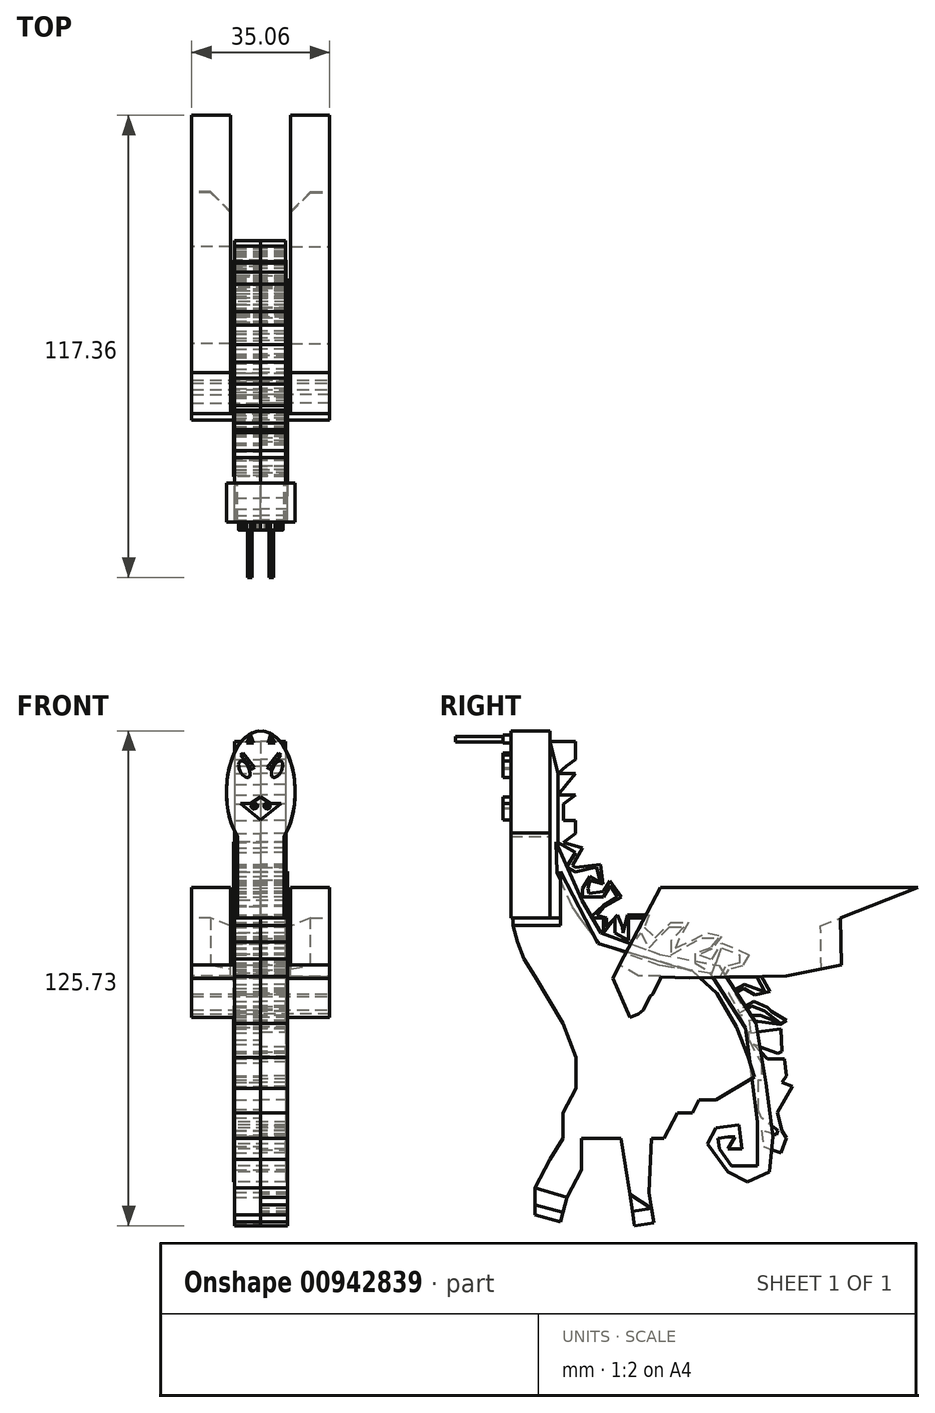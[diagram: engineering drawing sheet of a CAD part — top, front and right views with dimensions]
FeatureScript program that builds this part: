
annotation { "Feature Type Name" : "Feature", "Feature Type Description" : "" }
export const myFeature = defineFeature(function(context is Context, id is Id, definition is map)
    precondition{}
    {
        {
            var Q0;
            Q0=qCreatedBy(makeId("Front.planeOp"),FACE);
            var sketch = newSketch(context, id + "F0", { "sketchPlane" : qUnion([Q0])});
            skEllipse(sketch, "E0", {"center": v(0, 32.09) * mm, "majorRadius": 15.5 * mm, "minorRadius": 8.74 * mm, "majorAxis": v(0, -1)});
            skLineSegment(sketch, "E1", {"start": v(-6.45, 21.64) * mm, "end": v(-6.45, 0) * mm});
            skLineSegment(sketch, "E2", {"start": v(-6.45, 0) * mm, "end": v(5.95, 0) * mm});
            skLineSegment(sketch, "E3", {"start": v(5.95, 0) * mm, "end": v(5.95, 20.74) * mm});
            skSolve(sketch);
        }
        {
            var Q0;
            Q0=qCreatedBy(makeId("Front.planeOp"),FACE);
            var sketch = newSketch(context, id + "F1", { "sketchPlane" : qUnion([Q0])});
            skLineSegment(sketch, "E4", {"start": v(0, 30.81) * mm, "end": v(-2.55, 29.11) * mm});
            skLineSegment(sketch, "E5", {"start": v(-2.55, 29.11) * mm, "end": v(-5.1, 29.11) * mm});
            skLineSegment(sketch, "E6", {"start": v(-5.1, 29.11) * mm, "end": v(0, 24.86) * mm});
            skLineSegment(sketch, "E7", {"start": v(0, 29.11) * mm, "end": v(0, 30.81) * mm});
            skLineSegment(sketch, "E8", {"start": v(115.75, 36.4) * mm, "end": v(114.25, 37.64) * mm});
            skLineSegment(sketch, "E9", {"start": v(-5.09, 41.44) * mm, "end": v(-2.33, 37.83) * mm});
            skLineSegment(sketch, "E10", {"start": v(0, 29.11) * mm, "end": v(0, 24.86) * mm});
            skLineSegment(sketch, "E11", {"start": v(-2.54, 46.54) * mm, "end": v(-3.66, 44.54) * mm});
            skLineSegment(sketch, "E12", {"start": v(-3.66, 44.54) * mm, "end": v(-1.82, 44.54) * mm});
            skLineSegment(sketch, "E13", {"start": v(-1.82, 44.54) * mm, "end": v(-2.54, 46.54) * mm});
            skLineSegment(sketch, "E14", {"start": v(-5.09, 41.44) * mm, "end": v(-4.98, 41.6) * mm});
            skLineSegment(sketch, "E15", {"start": v(-4.98, 41.6) * mm, "end": v(-2.1, 37.83) * mm});
            skLineSegment(sketch, "E16", {"start": v(-2.1, 37.83) * mm, "end": v(-2.33, 37.83) * mm});
            skLineSegment(sketch, "E17", {"start": v(-4.49, 41.96) * mm, "end": v(-1.63, 38.23) * mm});
            skLineSegment(sketch, "E18", {"start": v(-1.63, 38.23) * mm, "end": v(-2.1, 37.83) * mm});
            skLineSegment(sketch, "E19", {"start": v(-4.49, 41.96) * mm, "end": v(-4.98, 41.6) * mm});
            skSolve(sketch);
        }
        {
            var Q0;
            Q0 = qSketchRegion(id + "F0", true);
            extrude(context, id + "F2", {"entities" : qUnion([Q0]), "depth" : 10 * mm, "offsetDistance" : 25.4 * mm});
        }
        {
            var Q0;
            Q0 = qSketchRegion(id + "F1", true);
            extrude(context, id + "F3", {"entities" : qUnion([Q0]), "depth" : 12 * mm, "offsetDistance" : 25.4 * mm});
        }
        {
            var Q0;
            Q0=makeQuery(id+"F3.opExtrude","SWEPT_BODY",BODY,{"disambiguationData":[OSD([sQuery(id+"F1.wireOp",EDGE,"E4"),sQuery(id+"F1.wireOp",EDGE,"E5"),sQuery(id+"F1.wireOp",EDGE,"E6"),sQuery(id+"F1.wireOp",EDGE,"E7"),sQuery(id+"F1.wireOp",EDGE,"E10")])]});
            var Q1;
            Q1=makeQuery(id+"F3.opExtrude","SWEPT_BODY",BODY,{"disambiguationData":[OSD([sQuery(id+"F1.wireOp",EDGE,"rFx2ZyDe-5tDm-OwJY-rhJK-uMzVgMLUW2AY")])]});
            var Q2;
            Q2=makeQuery(id+"F3.opExtrude","SWEPT_BODY",BODY,{"disambiguationData":[OSD([sQuery(id+"F1.wireOp",EDGE,"E9"),sQuery(id+"F1.wireOp",EDGE,"E14"),sQuery(id+"F1.wireOp",EDGE,"E16"),sQuery(id+"F1.wireOp",EDGE,"E17"),sQuery(id+"F1.wireOp",EDGE,"E18"),sQuery(id+"F1.wireOp",EDGE,"E19")])]});
            var Q3;
            Q3=makeQuery(id+"F3.opExtrude","SWEPT_BODY",BODY,{"disambiguationData":[OSD([sQuery(id+"F1.wireOp",EDGE,"E11"),sQuery(id+"F1.wireOp",EDGE,"E12"),sQuery(id+"F1.wireOp",EDGE,"E13")])]});
            var Q4;
            Q4=qCreatedBy(makeId("Right.planeOp"),FACE);
            mirror(context, id + "F4", {"operationType" : NewBodyOperationType.ADD, "entities" : qUnion([Q0, Q1, Q2, Q3]), "mirrorPlane" : qUnion([Q4])});
        }
        {
            var Q0;
            Q0=makeQuery(id+"F4.opPattern","COPY",FACE,{"derivedFrom":makeQuery(id+"F3.opExtrude","CAP_FACE",FACE,{"disambiguationData":[OSD([sQuery(id+"F1.wireOp",EDGE,"E11"),sQuery(id+"F1.wireOp",EDGE,"E12"),sQuery(id+"F1.wireOp",EDGE,"E13")])],"isStart":false}),"instanceName":"1"});
            var sketch = newSketch(context, id + "F5", { "sketchPlane" : qUnion([Q0])});
            skLineSegment(sketch, "E20", {"start": v(2.6, 46.13) * mm, "end": v(2.12, 44.79) * mm});
            skLineSegment(sketch, "E21", {"start": v(2.12, 44.79) * mm, "end": v(3.28, 44.79) * mm});
            skLineSegment(sketch, "E22", {"start": v(3.28, 44.79) * mm, "end": v(2.6, 46.13) * mm});
            skLineSegment(sketch, "E23", {"start": v(-2.57, 46.13) * mm, "end": v(-3.3, 44.79) * mm});
            skLineSegment(sketch, "E24", {"start": v(-3.3, 44.79) * mm, "end": v(-2.16, 44.79) * mm});
            skLineSegment(sketch, "E25", {"start": v(-2.16, 44.79) * mm, "end": v(-2.57, 46.13) * mm});
            skSolve(sketch);
        }
        {
            var Q0;
            Q0 = qSketchRegion(id + "F5", true);
            extrude(context, id + "F6", {"entities" : qUnion([Q0]), "depth" : 12 * mm, "offsetDistance" : 25.4 * mm});
        }
        {
            var Q0;
            {var subQ0=makeQuery(id+"F3.opExtrude","CAP_FACE",FACE,{"disambiguationData":[OSD([sQuery(id+"F1.wireOp",EDGE,"E4"),sQuery(id+"F1.wireOp",EDGE,"E5"),sQuery(id+"F1.wireOp",EDGE,"E6"),sQuery(id+"F1.wireOp",EDGE,"E7"),sQuery(id+"F1.wireOp",EDGE,"E10")])],"isStart":false});Q0=makeQuery(id+"F4.boolean.opBoolean","MERGE",FACE,{"derivedFrom":[subQ0,makeQuery(id+"F4.opPattern","COPY",FACE,{"derivedFrom":subQ0,"instanceName":"1"})]});}
            var sketch = newSketch(context, id + "F7", { "sketchPlane" : qUnion([Q0])});
            skCircle(sketch, "E26", {"center": v(-2.03, 28.28) * mm, "radius": 0.65 * mm});
            skCircle(sketch, "E27", {"center": v(1.78, 28.4) * mm, "radius": 0.63 * mm});
            skSolve(sketch);
        }
        {
            var Q0;
            Q0=qCreatedBy(makeId("Right.planeOp"),FACE);
            var sketch = newSketch(context, id + "F8", { "sketchPlane" : qUnion([Q0])});
            skLineSegment(sketch, "E28", {"start": v(1.53, 19.32) * mm, "end": v(8.1, 4.49) * mm});
            skLineSegment(sketch, "E29", {"start": v(8.1, 4.49) * mm, "end": v(12.92, -3.77) * mm});
            skLineSegment(sketch, "E30", {"start": v(12.92, -3.77) * mm, "end": v(27.76, -9.19) * mm});
            skLineSegment(sketch, "E31", {"start": v(27.76, -9.19) * mm, "end": v(42.82, -12.05) * mm});
            skLineSegment(sketch, "E32", {"start": v(42.82, -12.05) * mm, "end": v(52.23, -26.65) * mm});
            skLineSegment(sketch, "E33", {"start": v(52.23, -26.65) * mm, "end": v(54.87, -41.94) * mm});
            skLineSegment(sketch, "E34", {"start": v(54.87, -41.94) * mm, "end": v(56.65, -55.53) * mm});
            skLineSegment(sketch, "E35", {"start": v(56.65, -55.53) * mm, "end": v(55.76, -64.46) * mm});
            skPoint(sketch, "E35.endSnap0", {"position": v(55.76, -48.73) * mm});
            skLineSegment(sketch, "E36", {"start": v(55.76, -64.46) * mm, "end": v(50.13, -67.05) * mm});
            skLineSegment(sketch, "E37", {"start": v(50.13, -67.05) * mm, "end": v(45.17, -64.46) * mm});
            skLineSegment(sketch, "E38", {"start": v(45.17, -64.46) * mm, "end": v(40, -57.35) * mm});
            skLineSegment(sketch, "E39", {"start": v(40, -57.35) * mm, "end": v(42.06, -53.33) * mm});
            skLineSegment(sketch, "E40", {"start": v(42.06, -53.33) * mm, "end": v(47.98, -52.55) * mm});
            skLineSegment(sketch, "E41", {"start": v(47.98, -52.55) * mm, "end": v(48.77, -58.6) * mm});
            skLineSegment(sketch, "E42", {"start": v(48.77, -58.6) * mm, "end": v(45.17, -58.6) * mm});
            skLineSegment(sketch, "E43", {"start": v(45.17, -58.6) * mm, "end": v(46.97, -55.58) * mm});
            skPoint(sketch, "E43.endSnap0", {"position": v(48.38, -55.58) * mm});
            skPoint(sketch, "E43.endSnap1", {"position": v(46.97, -58.6) * mm});
            skLineSegment(sketch, "E44", {"start": v(46.97, -55.58) * mm, "end": v(45.17, -55.58) * mm});
            skLineSegment(sketch, "E45", {"start": v(45.17, -55.58) * mm, "end": v(42.6, -55.92) * mm});
            skLineSegment(sketch, "E46", {"start": v(42.6, -55.92) * mm, "end": v(42.95, -58.6) * mm});
            skLineSegment(sketch, "E47", {"start": v(42.95, -58.6) * mm, "end": v(46.1, -62.94) * mm});
            skLineSegment(sketch, "E48", {"start": v(46.1, -62.94) * mm, "end": v(52.7, -62.94) * mm});
            skLineSegment(sketch, "E49", {"start": v(52.7, -62.94) * mm, "end": v(52.7, -51.82) * mm});
            skLineSegment(sketch, "E50", {"start": v(52.7, -51.82) * mm, "end": v(51.42, -41.98) * mm});
            skLineSegment(sketch, "E51", {"start": v(51.42, -41.98) * mm, "end": v(49.57, -27.85) * mm});
            skLineSegment(sketch, "E52", {"start": v(49.57, -27.85) * mm, "end": v(40.66, -14.02) * mm});
            skLineSegment(sketch, "E53", {"start": v(40.66, -14.02) * mm, "end": v(27.76, -12.02) * mm});
            skLineSegment(sketch, "E54", {"start": v(27.76, -12.02) * mm, "end": v(12.6, -6.74) * mm});
            skLineSegment(sketch, "E55", {"start": v(12.6, -6.74) * mm, "end": v(5.63, 2.85) * mm});
            skLineSegment(sketch, "E56", {"start": v(5.63, 2.85) * mm, "end": v(1.76, 11.6) * mm});
            skLineSegment(sketch, "E57", {"start": v(1.53, 19.32) * mm, "end": v(1.76, 11.6) * mm});
            skSolve(sketch);
        }
        {
            var Q0;
            Q0 = qSketchRegion(id + "F8", true);
            extrude(context, id + "F9", {"entities" : qUnion([Q0]), "depth" : 6.45 * mm, "offsetDistance" : 25.4 * mm});
        }
        {
            var Q0;
            Q0 = qSketchRegion(id + "F8", true);
            extrude(context, id + "F10", {"entities" : qUnion([Q0]), "operationType" : NewBodyOperationType.ADD, "oppositeDirection" : true, "depth" : 6.86 * mm, "offsetDistance" : 25.4 * mm});
        }
        {
            var Q0;
            Q0=qCreatedBy(makeId("Right.planeOp"),FACE);
            var sketch = newSketch(context, id + "F11", { "sketchPlane" : qUnion([Q0])});
            skLineSegment(sketch, "E58", {"start": v(2.58, 11.8) * mm, "end": v(2.58, 0) * mm});
            skLineSegment(sketch, "E59", {"start": v(2.58, 0) * mm, "end": v(-9.48, 0) * mm});
            skLineSegment(sketch, "E60", {"start": v(-9.48, 0) * mm, "end": v(-9.48, -1.88) * mm});
            skLineSegment(sketch, "E61", {"start": v(-9.48, -1.88) * mm, "end": v(2.58, -1.88) * mm});
            skLineSegment(sketch, "E62", {"start": v(2.58, -1.88) * mm, "end": v(2.58, 0) * mm});
            skLineSegment(sketch, "E63", {"start": v(-9.48, -1.88) * mm, "end": v(-8.33, -6.04) * mm});
            skLineSegment(sketch, "E64", {"start": v(-8.33, -6.04) * mm, "end": v(-6.72, -10.35) * mm});
            skLineSegment(sketch, "E65", {"start": v(-6.72, -10.35) * mm, "end": v(-3.83, -14.8) * mm});
            skLineSegment(sketch, "E66", {"start": v(-3.83, -14.8) * mm, "end": v(0, -21.27) * mm});
            skLineSegment(sketch, "E67", {"start": v(0, -21.27) * mm, "end": v(3.22, -26.71) * mm});
            skLineSegment(sketch, "E68", {"start": v(3.22, -26.71) * mm, "end": v(6.59, -35.45) * mm});
            skLineSegment(sketch, "E69", {"start": v(6.59, -35.45) * mm, "end": v(6.59, -43.34) * mm});
            skLineSegment(sketch, "E70", {"start": v(6.59, -43.34) * mm, "end": v(3.22, -49.52) * mm});
            skLineSegment(sketch, "E71", {"start": v(3.22, -49.52) * mm, "end": v(3.22, -55.94) * mm});
            skLineSegment(sketch, "E72", {"start": v(3.22, -55.94) * mm, "end": v(0, -61.3) * mm});
            skLineSegment(sketch, "E73", {"start": v(0, -61.3) * mm, "end": v(-3.83, -68.55) * mm});
            skLineSegment(sketch, "E74", {"start": v(-3.83, -68.55) * mm, "end": v(-3.83, -75.4) * mm});
            skLineSegment(sketch, "E75", {"start": v(-3.83, -75.4) * mm, "end": v(2.58, -77.16) * mm});
            skLineSegment(sketch, "E76", {"start": v(2.58, -77.16) * mm, "end": v(3.22, -74.82) * mm});
            skLineSegment(sketch, "E77", {"start": v(3.22, -74.82) * mm, "end": v(-3.83, -72.89) * mm});
            skLineSegment(sketch, "E78", {"start": v(-3.83, -72.89) * mm, "end": v(3.22, -74.82) * mm});
            skLineSegment(sketch, "E79", {"start": v(3.22, -74.82) * mm, "end": v(4.27, -71.01) * mm});
            skLineSegment(sketch, "E80", {"start": v(4.27, -71.01) * mm, "end": v(-3.83, -68.55) * mm});
            skLineSegment(sketch, "E81", {"start": v(4.27, -71.01) * mm, "end": v(7.97, -64) * mm});
            skLineSegment(sketch, "E82", {"start": v(7.97, -64) * mm, "end": v(7.97, -55.94) * mm});
            skLineSegment(sketch, "E83", {"start": v(18, -55.94) * mm, "end": v(28.89, -55.94) * mm});
            skLineSegment(sketch, "E84", {"start": v(28.89, -55.94) * mm, "end": v(32.27, -49.52) * mm});
            skLineSegment(sketch, "E85", {"start": v(32.27, -49.52) * mm, "end": v(36.1, -49.52) * mm});
            skLineSegment(sketch, "E86", {"start": v(36.1, -49.52) * mm, "end": v(37.84, -46.23) * mm});
            skLineSegment(sketch, "E87", {"start": v(37.84, -46.23) * mm, "end": v(42.1, -46.23) * mm});
            skLineSegment(sketch, "E88", {"start": v(42.1, -46.23) * mm, "end": v(46.58, -43.57) * mm});
            skLineSegment(sketch, "E89", {"start": v(46.58, -43.57) * mm, "end": v(51.93, -40.4) * mm});
            skLineSegment(sketch, "E90", {"start": v(51.93, -40.4) * mm, "end": v(46.58, -43.57) * mm});
            skLineSegment(sketch, "E91", {"start": v(7.97, -55.94) * mm, "end": v(18, -55.94) * mm});
            skLineSegment(sketch, "E92", {"start": v(18, -55.94) * mm, "end": v(21.47, -78.15) * mm});
            skLineSegment(sketch, "E93", {"start": v(21.47, -78.15) * mm, "end": v(26.34, -77.39) * mm});
            skLineSegment(sketch, "E94", {"start": v(26.34, -77.39) * mm, "end": v(25.78, -73.8) * mm});
            skLineSegment(sketch, "E95", {"start": v(25.78, -73.8) * mm, "end": v(20.9, -74.56) * mm});
            skLineSegment(sketch, "E96", {"start": v(20.9, -74.56) * mm, "end": v(25.78, -73.8) * mm});
            skLineSegment(sketch, "E97", {"start": v(20.22, -70.14) * mm, "end": v(25.78, -73.8) * mm});
            skLineSegment(sketch, "E98", {"start": v(25.78, -73.8) * mm, "end": v(25.14, -69.67) * mm});
            skLineSegment(sketch, "E99", {"start": v(25.14, -69.67) * mm, "end": v(20.22, -70.14) * mm});
            skLineSegment(sketch, "E100", {"start": v(25.14, -69.67) * mm, "end": v(25.78, -55.94) * mm});
            skLineSegment(sketch, "E101", {"start": v(2.58, 11.8) * mm, "end": v(12.14, -6.48) * mm});
            skLineSegment(sketch, "E102", {"start": v(12.14, -6.48) * mm, "end": v(36.19, -13.45) * mm});
            skLineSegment(sketch, "E103", {"start": v(36.19, -13.45) * mm, "end": v(42.38, -19.18) * mm});
            skLineSegment(sketch, "E104", {"start": v(42.38, -19.18) * mm, "end": v(47.39, -27.63) * mm});
            skLineSegment(sketch, "E105", {"start": v(47.39, -27.63) * mm, "end": v(50.26, -35.08) * mm});
            skLineSegment(sketch, "E106", {"start": v(50.26, -35.08) * mm, "end": v(51.93, -40.4) * mm});
            skSolve(sketch);
        }
        {
            var Q0;
            Q0=makeQuery(id+"F11.imprint","IMPRINT",FACE,{"disambiguationData":[TD([[makeQuery(id+"F11.imprint","IMPRINT",EDGE,{"derivedFrom":sQuery(id+"F11.wireOp",EDGE,"E58")}),1.0]])]});
            var Q1;
            {var subQ2=sQuery(id+"F11.wireOp",EDGE,"E78");Q1=makeQuery(id+"F11.imprint","IMPRINT",FACE,{"disambiguationData":[TD([[makeQuery(id+"F11.imprint","IMPRINT",EDGE,{"derivedFrom":subQ2}),1.0]])]});}
            var Q2;
            {var subQ0=sQuery(id+"F11.wireOp",EDGE,"E75");Q2=makeQuery(id+"F11.imprint","IMPRINT",FACE,{"disambiguationData":[TD([[makeQuery(id+"F11.imprint","IMPRINT",EDGE,{"derivedFrom":subQ0}),1.0]])]});}
            var Q3;
            {var subQ4=sQuery(id+"F11.wireOp",EDGE,"E99");Q3=makeQuery(id+"F11.imprint","IMPRINT",FACE,{"disambiguationData":[TD([[makeQuery(id+"F11.imprint","IMPRINT",EDGE,{"derivedFrom":subQ4}),-1.0]])]});}
            var Q4;
            Q4=makeQuery(id+"F11.imprint","IMPRINT",FACE,{"disambiguationData":[TD([[makeQuery(id+"F11.imprint","IMPRINT",EDGE,{"derivedFrom":sQuery(id+"F11.wireOp",EDGE,"E97")}),1.0]])]});
            var Q5;
            {var subQ0=sQuery(id+"F11.wireOp",EDGE,"E96");Q5=makeQuery(id+"F11.imprint","IMPRINT",FACE,{"disambiguationData":[TD([[makeQuery(id+"F11.imprint","IMPRINT",EDGE,{"derivedFrom":subQ0}),1.0]])]});}
            var Q6;
            {var subQ0=sQuery(id+"F11.wireOp",EDGE,"E93");Q6=makeQuery(id+"F11.imprint","IMPRINT",FACE,{"disambiguationData":[TD([[makeQuery(id+"F11.imprint","IMPRINT",EDGE,{"derivedFrom":subQ0}),1.0]])]});}
            extrude(context, id + "F12", {"entities" : qUnion([Q0, Q1, Q2, Q3, Q4, Q5, Q6]), "operationType" : NewBodyOperationType.ADD, "depth" : 6.86 * mm, "offsetDistance" : 25.4 * mm});
        }
        {
            var Q0;
            Q0 = qSketchRegion(id + "F11", true);
            extrude(context, id + "F13", {"entities" : qUnion([Q0]), "oppositeDirection" : true, "depth" : 6.6 * mm, "offsetDistance" : 25.4 * mm});
        }
        {
            var Q0;
            Q0=qCreatedBy(makeId("Right.planeOp"),FACE);
            var sketch = newSketch(context, id + "F14", { "sketchPlane" : qUnion([Q0])});
            skLineSegment(sketch, "E107", {"start": v(15.93, -15.4) * mm, "end": v(20.23, -25.3) * mm});
            skLineSegment(sketch, "E108", {"start": v(20.23, -25.3) * mm, "end": v(22.44, -24.34) * mm});
            skLineSegment(sketch, "E109", {"start": v(22.44, -24.34) * mm, "end": v(25.61, -21.85) * mm});
            skLineSegment(sketch, "E110", {"start": v(25.61, -21.85) * mm, "end": v(25.61, -19.7) * mm});
            skLineSegment(sketch, "E111", {"start": v(25.61, -19.7) * mm, "end": v(27.98, -17.76) * mm});
            skLineSegment(sketch, "E112", {"start": v(27.98, -14.75) * mm, "end": v(25.61, -14.75) * mm});
            skLineSegment(sketch, "E113", {"start": v(25.61, -14.75) * mm, "end": v(22.44, -14.75) * mm});
            skLineSegment(sketch, "E114", {"start": v(22.44, -14.75) * mm, "end": v(17.65, -11.95) * mm});
            skLineSegment(sketch, "E115", {"start": v(17.65, -11.95) * mm, "end": v(15.93, -15.4) * mm});
            skLineSegment(sketch, "E116", {"start": v(27.98, -14.75) * mm, "end": v(27.98, -17.76) * mm});
            skSolve(sketch);
        }
        {
            var Q0;
            Q0 = qSketchRegion(id + "F14", true);
            extrude(context, id + "F15", {"entities" : qUnion([Q0]), "depth" : 17.53 * mm, "offsetDistance" : 25.4 * mm});
        }
        {
            var Q0;
            Q0=makeQuery(id+"F15.opExtrude","CAP_FACE",FACE,{"disambiguationData":[OSD([sQuery(id+"F14.wireOp",EDGE,"E107"),sQuery(id+"F14.wireOp",EDGE,"E108"),sQuery(id+"F14.wireOp",EDGE,"E109"),sQuery(id+"F14.wireOp",EDGE,"E110"),sQuery(id+"F14.wireOp",EDGE,"E111"),sQuery(id+"F14.wireOp",EDGE,"E112"),sQuery(id+"F14.wireOp",EDGE,"E113"),sQuery(id+"F14.wireOp",EDGE,"E114"),sQuery(id+"F14.wireOp",EDGE,"E115"),sQuery(id+"F14.wireOp",EDGE,"E116")])],"isStart":false});
            var sketch = newSketch(context, id + "F16", { "sketchPlane" : qUnion([Q0])});
            skLineSegment(sketch, "E117", {"start": v(20.04, -15.4) * mm, "end": v(59.98, -14.75) * mm});
            skPoint(sketch, "E117.startSnap0", {"position": v(20.04, -13.35) * mm});
            skLineSegment(sketch, "E118", {"start": v(59.98, -14.75) * mm, "end": v(73.95, -11.95) * mm});
            skLineSegment(sketch, "E119", {"start": v(73.95, -11.95) * mm, "end": v(73.76, 0) * mm});
            skLineSegment(sketch, "E120", {"start": v(73.76, 0) * mm, "end": v(93.36, 7.8) * mm});
            skLineSegment(sketch, "E121", {"start": v(93.36, 7.8) * mm, "end": v(27.98, 7.8) * mm});
            skLineSegment(sketch, "E122", {"start": v(27.98, 7.8) * mm, "end": v(17.65, -11.95) * mm});
            skLineSegment(sketch, "E123", {"start": v(17.65, -11.95) * mm, "end": v(22.44, -14.75) * mm});
            skLineSegment(sketch, "E124", {"start": v(22.44, -14.75) * mm, "end": v(35.37, -15.15) * mm});
            skLineSegment(sketch, "E125", {"start": v(41.59, -15.05) * mm, "end": v(46.16, -14.97) * mm});
            skSolve(sketch);
        }
        {
            var Q0;
            Q0 = qSketchRegion(id + "F16", true);
            extrude(context, id + "F17", {"entities" : qUnion([Q0]), "operationType" : NewBodyOperationType.ADD, "oppositeDirection" : true, "depth" : 9.9 * mm, "offsetDistance" : 25.4 * mm});
        }
        {
            var Q0;
            Q0=makeQuery(id+"F15.opExtrude","SWEPT_BODY",BODY,{"disambiguationData":[OSD([sQuery(id+"F14.wireOp",EDGE,"E107"),sQuery(id+"F14.wireOp",EDGE,"E108"),sQuery(id+"F14.wireOp",EDGE,"E109"),sQuery(id+"F14.wireOp",EDGE,"E110"),sQuery(id+"F14.wireOp",EDGE,"E111"),sQuery(id+"F14.wireOp",EDGE,"E112"),sQuery(id+"F14.wireOp",EDGE,"E113"),sQuery(id+"F14.wireOp",EDGE,"E114"),sQuery(id+"F14.wireOp",EDGE,"E115"),sQuery(id+"F14.wireOp",EDGE,"E116")])]});
            var Q1;
            Q1=qCreatedBy(makeId("Right.planeOp"),FACE);
            mirror(context, id + "F18", {"entities" : qUnion([Q0]), "mirrorPlane" : qUnion([Q1])});
        }
        {
            var Q0;
            Q0=makeQuery(id+"F7.imprint","IMPRINT",FACE,{"disambiguationData":[TD([[makeQuery(id+"F7.imprint","IMPRINT",EDGE,{"derivedFrom":sQuery(id+"F7.wireOp",EDGE,"E27")}),1.0]])]});
            var Q1;
            Q1=sQuery(id+"F7.wireOp",EDGE,"E27");
            extrude(context, id + "F19", {"entities" : qUnion([Q0]), "operationType" : NewBodyOperationType.REMOVE, "surfaceEntities" : qUnion([Q1]), "oppositeDirection" : true, "depth" : 2 * mm, "offsetDistance" : 25.4 * mm});
        }
        {
            var Q0;
            {var subQ0=makeQuery(id+"F3.opExtrude","CAP_FACE",FACE,{"disambiguationData":[OSD([sQuery(id+"F1.wireOp",EDGE,"E4"),sQuery(id+"F1.wireOp",EDGE,"E5"),sQuery(id+"F1.wireOp",EDGE,"E6"),sQuery(id+"F1.wireOp",EDGE,"E7"),sQuery(id+"F1.wireOp",EDGE,"E10")])],"isStart":false});Q0=makeQuery(id+"F4.boolean.opBoolean","MERGE",FACE,{"derivedFrom":[subQ0,makeQuery(id+"F4.opPattern","COPY",FACE,{"derivedFrom":subQ0,"instanceName":"1"})]});}
            var sketch = newSketch(context, id + "F20", { "sketchPlane" : qUnion([Q0])});
            skCircle(sketch, "E126", {"center": v(-1.46, 28.48) * mm, "radius": 0.65 * mm});
            skSolve(sketch);
        }
        {
            var Q0;
            Q0=makeQuery(id+"F20.imprint","IMPRINT",FACE,{"disambiguationData":[TD([[makeQuery(id+"F20.imprint","IMPRINT",EDGE,{"derivedFrom":sQuery(id+"F20.wireOp",EDGE,"E126")}),1.0]])]});
            extrude(context, id + "F21", {"entities" : qUnion([Q0]), "operationType" : NewBodyOperationType.REMOVE, "oppositeDirection" : true, "depth" : 2 * mm, "offsetDistance" : 25.4 * mm});
        }
        {
            var Q0;
            Q0=qCreatedBy(makeId("Right.planeOp"),FACE);
            var sketch = newSketch(context, id + "F22", { "sketchPlane" : qUnion([Q0])});
            skLineSegment(sketch, "E127", {"start": v(0, 44.82) * mm, "end": v(6.37, 44.82) * mm});
            skLineSegment(sketch, "E128", {"start": v(6.37, 44.82) * mm, "end": v(6.37, 42.84) * mm});
            skLineSegment(sketch, "E129", {"start": v(6.37, 42.84) * mm, "end": v(6.37, 40.27) * mm});
            skLineSegment(sketch, "E130", {"start": v(6.37, 40.27) * mm, "end": v(4.19, 38.62) * mm});
            skLineSegment(sketch, "E131", {"start": v(4.19, 38.62) * mm, "end": v(2.01, 36.76) * mm});
            skLineSegment(sketch, "E132", {"start": v(2.01, 36.76) * mm, "end": v(6.37, 36.76) * mm});
            skLineSegment(sketch, "E133", {"start": v(6.37, 36.76) * mm, "end": v(4.19, 33.94) * mm});
            skLineSegment(sketch, "E134", {"start": v(4.19, 33.94) * mm, "end": v(2.01, 31.34) * mm});
            skLineSegment(sketch, "E135", {"start": v(2.01, 31.34) * mm, "end": v(6.37, 31.34) * mm});
            skLineSegment(sketch, "E136", {"start": v(6.37, 31.34) * mm, "end": v(2.01, 27.92) * mm});
            skLineSegment(sketch, "E137", {"start": v(2.01, 27.92) * mm, "end": v(2.01, 24.86) * mm});
            skLineSegment(sketch, "E138", {"start": v(2.01, 24.86) * mm, "end": v(6.37, 24.86) * mm});
            skLineSegment(sketch, "E139", {"start": v(6.37, 24.86) * mm, "end": v(6.37, 21.51) * mm});
            skLineSegment(sketch, "E140", {"start": v(6.37, 21.51) * mm, "end": v(2.01, 19.24) * mm});
            skLineSegment(sketch, "E141", {"start": v(2.01, 19.24) * mm, "end": v(6.37, 16.68) * mm});
            skLineSegment(sketch, "E142", {"start": v(6.37, 16.68) * mm, "end": v(4.19, 12.95) * mm});
            skLineSegment(sketch, "E143", {"start": v(4.19, 12.95) * mm, "end": v(6.37, 11.67) * mm});
            skLineSegment(sketch, "E144", {"start": v(6.37, 11.67) * mm, "end": v(11.8, 12.95) * mm});
            skLineSegment(sketch, "E145", {"start": v(11.8, 12.95) * mm, "end": v(12.73, 9.06) * mm});
            skLineSegment(sketch, "E146", {"start": v(12.73, 9.06) * mm, "end": v(10.06, 10.62) * mm});
            skLineSegment(sketch, "E147", {"start": v(10.06, 10.62) * mm, "end": v(8.24, 7.5) * mm});
            skLineSegment(sketch, "E148", {"start": v(8.24, 7.5) * mm, "end": v(8.24, 5.33) * mm});
            skLineSegment(sketch, "E149", {"start": v(8.24, 5.33) * mm, "end": v(13.56, 5.33) * mm});
            skLineSegment(sketch, "E150", {"start": v(13.56, 5.33) * mm, "end": v(15.33, 8.35) * mm});
            skLineSegment(sketch, "E151", {"start": v(15.33, 8.35) * mm, "end": v(17.11, 5.33) * mm});
            skLineSegment(sketch, "E152", {"start": v(17.11, 5.33) * mm, "end": v(13.56, 3.24) * mm});
            skLineSegment(sketch, "E153", {"start": v(13.56, 0) * mm, "end": v(10.14, 0) * mm});
            skLineSegment(sketch, "E154", {"start": v(10.14, 0) * mm, "end": v(13.56, 3.24) * mm});
            skLineSegment(sketch, "E155", {"start": v(13.56, 0) * mm, "end": v(13.56, -3.72) * mm});
            skLineSegment(sketch, "E156", {"start": v(16.5, 0) * mm, "end": v(13.56, -3.72) * mm});
            skLineSegment(sketch, "E157", {"start": v(16.5, 0) * mm, "end": v(16.5, -3.72) * mm});
            skLineSegment(sketch, "E158", {"start": v(16.5, -3.72) * mm, "end": v(19.86, -5.7) * mm});
            skLineSegment(sketch, "E159", {"start": v(19.86, -5.7) * mm, "end": v(19.86, 0) * mm});
            skLineSegment(sketch, "E160", {"start": v(19.86, 0) * mm, "end": v(23.9, 0) * mm});
            skLineSegment(sketch, "E161", {"start": v(23.9, 0) * mm, "end": v(21.89, -5.29) * mm});
            skPoint(sketch, "E161.endSnap0", {"position": v(21.89, 0) * mm});
            skLineSegment(sketch, "E162", {"start": v(21.89, -5.29) * mm, "end": v(23.12, -3.72) * mm});
            skLineSegment(sketch, "E163", {"start": v(23.12, -3.72) * mm, "end": v(25.1, -7.6) * mm});
            skLineSegment(sketch, "E164", {"start": v(25.1, -7.6) * mm, "end": v(30.34, -2.2) * mm});
            skLineSegment(sketch, "E165", {"start": v(30.34, -2.2) * mm, "end": v(34, -2.2) * mm});
            skLineSegment(sketch, "E166", {"start": v(34, -2.2) * mm, "end": v(30.69, -5.76) * mm});
            skLineSegment(sketch, "E167", {"start": v(30.69, -5.76) * mm, "end": v(30.69, -9.32) * mm});
            skLineSegment(sketch, "E168", {"start": v(30.69, -9.32) * mm, "end": v(38.59, -5) * mm});
            skLineSegment(sketch, "E169", {"start": v(38.59, -5) * mm, "end": v(42.7, -5) * mm});
            skLineSegment(sketch, "E170", {"start": v(42.7, -5) * mm, "end": v(40.73, -7.6) * mm});
            skLineSegment(sketch, "E171", {"start": v(40.73, -7.6) * mm, "end": v(36.75, -8.96) * mm});
            skLineSegment(sketch, "E172", {"start": v(36.75, -8.96) * mm, "end": v(36.75, -11.39) * mm});
            skLineSegment(sketch, "E173", {"start": v(36.75, -11.39) * mm, "end": v(41.08, -14.1) * mm});
            skLineSegment(sketch, "E174", {"start": v(41.08, -14.1) * mm, "end": v(43.56, -7.6) * mm});
            skLineSegment(sketch, "E175", {"start": v(43.56, -7.6) * mm, "end": v(48.06, -9.32) * mm});
            skLineSegment(sketch, "E176", {"start": v(48.06, -9.32) * mm, "end": v(48.06, -11.39) * mm});
            skLineSegment(sketch, "E177", {"start": v(48.06, -11.39) * mm, "end": v(44.42, -12.41) * mm});
            skLineSegment(sketch, "E178", {"start": v(44.42, -12.41) * mm, "end": v(43.15, -14.98) * mm});
            skLineSegment(sketch, "E179", {"start": v(43.15, -14.98) * mm, "end": v(52.48, -14.98) * mm});
            skLineSegment(sketch, "E180", {"start": v(52.48, -14.98) * mm, "end": v(54.55, -18.77) * mm});
            skLineSegment(sketch, "E181", {"start": v(54.55, -18.77) * mm, "end": v(49.4, -16.8) * mm});
            skLineSegment(sketch, "E182", {"start": v(49.4, -16.8) * mm, "end": v(45.35, -19.03) * mm});
            skLineSegment(sketch, "E183", {"start": v(45.35, -19.03) * mm, "end": v(48.1, -24.04) * mm});
            skLineSegment(sketch, "E184", {"start": v(48.1, -24.04) * mm, "end": v(51.13, -22.38) * mm});
            skLineSegment(sketch, "E185", {"start": v(51.13, -22.38) * mm, "end": v(54.39, -23.63) * mm});
            skLineSegment(sketch, "E186", {"start": v(54.39, -23.63) * mm, "end": v(58.42, -26.67) * mm});
            skLineSegment(sketch, "E187", {"start": v(58.42, -26.67) * mm, "end": v(53.48, -24.78) * mm});
            skLineSegment(sketch, "E188", {"start": v(53.48, -24.78) * mm, "end": v(48.1, -24.78) * mm});
            skLineSegment(sketch, "E189", {"start": v(48.1, -24.78) * mm, "end": v(50.49, -29.16) * mm});
            skLineSegment(sketch, "E190", {"start": v(50.49, -29.16) * mm, "end": v(58.37, -29.16) * mm});
            skLineSegment(sketch, "E191", {"start": v(58.37, -29.16) * mm, "end": v(58.37, -33.96) * mm});
            skLineSegment(sketch, "E192", {"start": v(58.37, -33.96) * mm, "end": v(54.4, -32.44) * mm});
            skLineSegment(sketch, "E193", {"start": v(54.4, -32.44) * mm, "end": v(50.49, -30.94) * mm});
            skLineSegment(sketch, "E194", {"start": v(50.49, -30.94) * mm, "end": v(53.66, -36.74) * mm});
            skLineSegment(sketch, "E195", {"start": v(53.66, -36.74) * mm, "end": v(58.49, -40.39) * mm});
            skLineSegment(sketch, "E196", {"start": v(58.49, -40.39) * mm, "end": v(58.49, -36.68) * mm});
            skLineSegment(sketch, "E197", {"start": v(58.49, -36.68) * mm, "end": v(53.66, -36.74) * mm});
            skLineSegment(sketch, "E198", {"start": v(53.66, -41.17) * mm, "end": v(57.73, -48.59) * mm});
            skLineSegment(sketch, "E199", {"start": v(57.73, -48.59) * mm, "end": v(59.96, -42.74) * mm});
            skLineSegment(sketch, "E200", {"start": v(59.96, -42.74) * mm, "end": v(53.66, -41.17) * mm});
            skLineSegment(sketch, "E201", {"start": v(53.66, -36.74) * mm, "end": v(53.66, -41.17) * mm});
            skLineSegment(sketch, "E202", {"start": v(50.49, -30.94) * mm, "end": v(50.49, -29.16) * mm});
            skLineSegment(sketch, "E203", {"start": v(52.8, -41.17) * mm, "end": v(52.8, -48.65) * mm});
            skLineSegment(sketch, "E204", {"start": v(52.8, -48.65) * mm, "end": v(57.82, -50.57) * mm});
            skLineSegment(sketch, "E205", {"start": v(57.82, -50.57) * mm, "end": v(57.82, -53.93) * mm});
            skLineSegment(sketch, "E206", {"start": v(57.82, -53.93) * mm, "end": v(53.66, -50.8) * mm});
            skLineSegment(sketch, "E207", {"start": v(53.66, -50.8) * mm, "end": v(52.8, -48.65) * mm});
            skLineSegment(sketch, "E208", {"start": v(53.66, -53.93) * mm, "end": v(54.21, -58.04) * mm});
            skLineSegment(sketch, "E209", {"start": v(54.21, -58.04) * mm, "end": v(58.6, -59.71) * mm});
            skLineSegment(sketch, "E210", {"start": v(58.6, -59.71) * mm, "end": v(60.08, -55.86) * mm});
            skLineSegment(sketch, "E211", {"start": v(60.08, -55.86) * mm, "end": v(53.66, -53.93) * mm});
            skLineSegment(sketch, "E212", {"start": v(52.8, -41.17) * mm, "end": v(53.94, -41.17) * mm});
            skPoint(sketch, "E212.endSnap0", {"position": v(53.94, -55.99) * mm});
            skLineSegment(sketch, "E213", {"start": v(53.94, -41.17) * mm, "end": v(58.49, -40.39) * mm});
            skLineSegment(sketch, "E214", {"start": v(6.37, 42.84) * mm, "end": v(6.37, 44.82) * mm});
            skLineSegment(sketch, "E215", {"start": v(0, 44.82) * mm, "end": v(2.01, 36.76) * mm});
            skLineSegment(sketch, "E216", {"start": v(2.01, 36.76) * mm, "end": v(2.01, 31.34) * mm});
            skLineSegment(sketch, "E217", {"start": v(2.01, 31.34) * mm, "end": v(2.01, 27.92) * mm});
            skLineSegment(sketch, "E218", {"start": v(2.01, 24.86) * mm, "end": v(2.01, 19.24) * mm});
            skLineSegment(sketch, "E219", {"start": v(3.32, 28.94) * mm, "end": v(3.32, 24.86) * mm});
            skLineSegment(sketch, "E220", {"start": v(3.32, 19.24) * mm, "end": v(8.24, 17.76) * mm});
            skLineSegment(sketch, "E221", {"start": v(8.24, 17.76) * mm, "end": v(5.67, 13.37) * mm});
            skLineSegment(sketch, "E222", {"start": v(5.67, 13.37) * mm, "end": v(6.37, 12.84) * mm});
            skLineSegment(sketch, "E223", {"start": v(6.37, 12.84) * mm, "end": v(12.71, 13.68) * mm});
            skLineSegment(sketch, "E224", {"start": v(12.71, 13.68) * mm, "end": v(13.38, 8.72) * mm});
            skLineSegment(sketch, "E225", {"start": v(13.38, 8.72) * mm, "end": v(10.14, 9.53) * mm});
            skLineSegment(sketch, "E226", {"start": v(10.14, 9.53) * mm, "end": v(9.63, 7.5) * mm});
            skLineSegment(sketch, "E227", {"start": v(9.63, 7.5) * mm, "end": v(9.8, 6.2) * mm});
            skLineSegment(sketch, "E228", {"start": v(9.8, 6.2) * mm, "end": v(13.56, 6.7) * mm});
            skLineSegment(sketch, "E229", {"start": v(13.56, 6.7) * mm, "end": v(15.13, 9.38) * mm});
            skLineSegment(sketch, "E230", {"start": v(15.13, 9.38) * mm, "end": v(18.08, 5.33) * mm});
            skLineSegment(sketch, "E231", {"start": v(18.08, 5.33) * mm, "end": v(13.85, 3.01) * mm});
            skLineSegment(sketch, "E232", {"start": v(13.85, 3.01) * mm, "end": v(11.84, 0.6) * mm});
            skLineSegment(sketch, "E233", {"start": v(11.84, 0.6) * mm, "end": v(14.27, 0) * mm});
            skLineSegment(sketch, "E234", {"start": v(14.27, 0) * mm, "end": v(14.27, -2.2) * mm});
            skLineSegment(sketch, "E235", {"start": v(14.27, -2.2) * mm, "end": v(17.11, 0.75) * mm});
            skLineSegment(sketch, "E236", {"start": v(17.11, 0.75) * mm, "end": v(18.3, -2.2) * mm});
            skLineSegment(sketch, "E237", {"start": v(18.3, -2.2) * mm, "end": v(18.5, -3.72) * mm});
            skLineSegment(sketch, "E238", {"start": v(18.5, -3.72) * mm, "end": v(19.63, 0.75) * mm});
            skLineSegment(sketch, "E239", {"start": v(19.63, 0.75) * mm, "end": v(25.1, 0.75) * mm});
            skLineSegment(sketch, "E240", {"start": v(25.1, 0.75) * mm, "end": v(23.9, -2.38) * mm});
            skLineSegment(sketch, "E241", {"start": v(23.9, -2.38) * mm, "end": v(26.62, -5) * mm});
            skLineSegment(sketch, "E242", {"start": v(26.62, -5) * mm, "end": v(30.69, -1.15) * mm});
            skLineSegment(sketch, "E243", {"start": v(30.69, -1.15) * mm, "end": v(35.13, -1.15) * mm});
            skLineSegment(sketch, "E244", {"start": v(35.13, -1.15) * mm, "end": v(32.7, -5.29) * mm});
            skLineSegment(sketch, "E245", {"start": v(32.7, -5.29) * mm, "end": v(31.88, -7.6) * mm});
            skLineSegment(sketch, "E246", {"start": v(31.88, -7.6) * mm, "end": v(40.03, -3.72) * mm});
            skLineSegment(sketch, "E247", {"start": v(40.03, -3.72) * mm, "end": v(43.56, -4.6) * mm});
            skLineSegment(sketch, "E248", {"start": v(43.56, -4.6) * mm, "end": v(41.08, -7.9) * mm});
            skLineSegment(sketch, "E249", {"start": v(41.08, -7.9) * mm, "end": v(37.87, -9.32) * mm});
            skLineSegment(sketch, "E250", {"start": v(37.87, -9.32) * mm, "end": v(41.08, -10.55) * mm});
            skLineSegment(sketch, "E251", {"start": v(41.08, -10.55) * mm, "end": v(43.56, -6.3) * mm});
            skLineSegment(sketch, "E252", {"start": v(43.56, -6.3) * mm, "end": v(50.49, -9.32) * mm});
            skLineSegment(sketch, "E253", {"start": v(3.32, 19.24) * mm, "end": v(6.37, 21.51) * mm});
            skLineSegment(sketch, "E254", {"start": v(50.49, -9.32) * mm, "end": v(48.8, -12.2) * mm});
            skLineSegment(sketch, "E255", {"start": v(48.8, -12.2) * mm, "end": v(45.26, -13.03) * mm});
            skLineSegment(sketch, "E256", {"start": v(45.26, -13.03) * mm, "end": v(44.31, -14.65) * mm});
            skLineSegment(sketch, "E257", {"start": v(44.31, -14.65) * mm, "end": v(53.57, -14.65) * mm});
            skLineSegment(sketch, "E258", {"start": v(53.57, -14.65) * mm, "end": v(55.78, -18.69) * mm});
            skLineSegment(sketch, "E259", {"start": v(55.78, -18.69) * mm, "end": v(52.01, -19.58) * mm});
            skLineSegment(sketch, "E260", {"start": v(52.01, -19.58) * mm, "end": v(49.17, -17.91) * mm});
            skLineSegment(sketch, "E261", {"start": v(49.17, -17.91) * mm, "end": v(46.97, -19.11) * mm});
            skLineSegment(sketch, "E262", {"start": v(46.97, -19.11) * mm, "end": v(48.96, -22.75) * mm});
            skLineSegment(sketch, "E263", {"start": v(48.96, -22.75) * mm, "end": v(51.75, -21.22) * mm});
            skLineSegment(sketch, "E264", {"start": v(51.75, -21.22) * mm, "end": v(55.15, -22.7) * mm});
            skLineSegment(sketch, "E265", {"start": v(55.15, -22.7) * mm, "end": v(56.17, -23.76) * mm});
            skLineSegment(sketch, "E266", {"start": v(56.17, -23.76) * mm, "end": v(60.08, -26.05) * mm});
            skLineSegment(sketch, "E267", {"start": v(60.08, -26.05) * mm, "end": v(58.42, -26.96) * mm});
            skLineSegment(sketch, "E268", {"start": v(58.42, -26.96) * mm, "end": v(50.49, -25.92) * mm});
            skLineSegment(sketch, "E269", {"start": v(50.49, -25.92) * mm, "end": v(50.92, -29.16) * mm});
            skLineSegment(sketch, "E270", {"start": v(50.92, -29.16) * mm, "end": v(58.6, -28.13) * mm});
            skLineSegment(sketch, "E271", {"start": v(58.6, -28.13) * mm, "end": v(58.86, -33.9) * mm});
            skLineSegment(sketch, "E272", {"start": v(58.86, -33.9) * mm, "end": v(57.9, -34.44) * mm});
            skLineSegment(sketch, "E273", {"start": v(57.9, -34.44) * mm, "end": v(51.68, -32.06) * mm});
            skLineSegment(sketch, "E274", {"start": v(51.68, -32.06) * mm, "end": v(55.15, -35.76) * mm});
            skLineSegment(sketch, "E275", {"start": v(55.15, -35.76) * mm, "end": v(59.5, -35.76) * mm});
            skLineSegment(sketch, "E276", {"start": v(59.5, -35.76) * mm, "end": v(60.08, -40.08) * mm});
            skLineSegment(sketch, "E277", {"start": v(60.08, -40.08) * mm, "end": v(58.86, -41.7) * mm});
            skLineSegment(sketch, "E278", {"start": v(58.86, -41.7) * mm, "end": v(61.6, -42.74) * mm});
            skLineSegment(sketch, "E279", {"start": v(61.6, -42.74) * mm, "end": v(57.73, -49.33) * mm});
            skLineSegment(sketch, "E280", {"start": v(57.73, -49.33) * mm, "end": v(58.86, -54.13) * mm});
            skLineSegment(sketch, "E281", {"start": v(58.86, -54.13) * mm, "end": v(60.08, -55.86) * mm});
            skLineSegment(sketch, "E282", {"start": v(57.82, -53.93) * mm, "end": v(57.24, -55.86) * mm});
            skLineSegment(sketch, "E283", {"start": v(57.24, -55.86) * mm, "end": v(58.86, -54.13) * mm});
            skSolve(sketch);
        }
        {
            var Q0;
            Q0 = qSketchRegion(id + "F22", true);
            extrude(context, id + "F23", {"entities" : qUnion([Q0]), "operationType" : NewBodyOperationType.ADD, "depth" : 6.35 * mm, "offsetDistance" : 25.4 * mm});
        }
        {
            var Q0;
            Q0 = qSketchRegion(id + "F22", true);
            extrude(context, id + "F24", {"entities" : qUnion([Q0]), "oppositeDirection" : true, "depth" : 6.6 * mm, "offsetDistance" : 25.4 * mm});
        }
        {
            var Q0;
            Q0=makeQuery(id+"F17.opExtrude","CAP_EDGE",EDGE,{"disambiguationData":[OSD([sQuery(id+"F16.wireOp",EDGE,"E119")])],"isStart":false});
            var Q1;
            Q1=makeQuery(id+"F18.opPattern","COPY",EDGE,{"derivedFrom":makeQuery(id+"F17.opExtrude","CAP_EDGE",EDGE,{"disambiguationData":[OSD([sQuery(id+"F16.wireOp",EDGE,"E119")])],"isStart":false}),"instanceName":"1"});
            var Q2;
            Q2=makeQuery(id+"F15.opExtrude","SWEPT_EDGE",EDGE,{"disambiguationData":[OSD([sQuery(id+"F14.wireOp",EDGE,"E111"),sQuery(id+"F14.wireOp",EDGE,"E116")])]});
            var Q3;
            Q3=makeQuery(id+"F15.opExtrude","SWEPT_EDGE",EDGE,{"disambiguationData":[OSD([sQuery(id+"F14.wireOp",EDGE,"E109"),sQuery(id+"F14.wireOp",EDGE,"E110")])]});
            var Q4;
            Q4=makeQuery(id+"F18.opPattern","COPY",EDGE,{"derivedFrom":makeQuery(id+"F15.opExtrude","SWEPT_EDGE",EDGE,{"disambiguationData":[OSD([sQuery(id+"F14.wireOp",EDGE,"E111"),sQuery(id+"F14.wireOp",EDGE,"E116")])]}),"instanceName":"1"});
            var Q5;
            Q5=makeQuery(id+"F18.opPattern","COPY",EDGE,{"derivedFrom":makeQuery(id+"F15.opExtrude","SWEPT_EDGE",EDGE,{"disambiguationData":[OSD([sQuery(id+"F14.wireOp",EDGE,"E109"),sQuery(id+"F14.wireOp",EDGE,"E110")])]}),"instanceName":"1"});
            chamfer(context, id + "F25", {"entities" : qUnion([Q0, Q1, Q2, Q3, Q4, Q5]), "width" : 5.08 * mm, "tangentPropagation" : true});
        }
        {
            var Q0;
            Q0=makeQuery(id+"F2.opExtrude","CAP_FACE",FACE,{"disambiguationData":[OSD([sQuery(id+"F0.wireOp",EDGE,"E0"),sQuery(id+"F0.wireOp",EDGE,"E1"),sQuery(id+"F0.wireOp",EDGE,"E2"),sQuery(id+"F0.wireOp",EDGE,"E3")])],"isStart":false});
            var sketch = newSketch(context, id + "F26", { "sketchPlane" : qUnion([Q0])});
            skEllipse(sketch, "E284", {"center": v(-4.16, 37.8) * mm, "majorRadius": 2.27 * mm, "minorRadius": 1.14 * mm, "majorAxis": v(0.45, -0.9)});
            skSolve(sketch);
        }
        {
            var Q0;
            Q0=makeQuery(id+"F26.imprint","IMPRINT",FACE,{"disambiguationData":[TD([[makeQuery(id+"F26.imprint","IMPRINT",EDGE,{"derivedFrom":sQuery(id+"F26.wireOp",EDGE,"E284")}),1.0]])]});
            extrude(context, id + "F27", {"entities" : qUnion([Q0]), "operationType" : NewBodyOperationType.ADD, "depth" : 2 * mm, "offsetDistance" : 25.4 * mm});
        }
        {
            var Q0;
            Q0=makeQuery(id+"F2.opExtrude","SWEPT_BODY",BODY,{"disambiguationData":[OSD([sQuery(id+"F0.wireOp",EDGE,"E0"),sQuery(id+"F0.wireOp",EDGE,"E1"),sQuery(id+"F0.wireOp",EDGE,"E2"),sQuery(id+"F0.wireOp",EDGE,"E3")])]});
            var Q1;
            Q1=qCreatedBy(makeId("Right.planeOp"),FACE);
            mirror(context, id + "F28", {"entities" : qUnion([Q0]), "mirrorPlane" : qUnion([Q1])});
        }
    });
